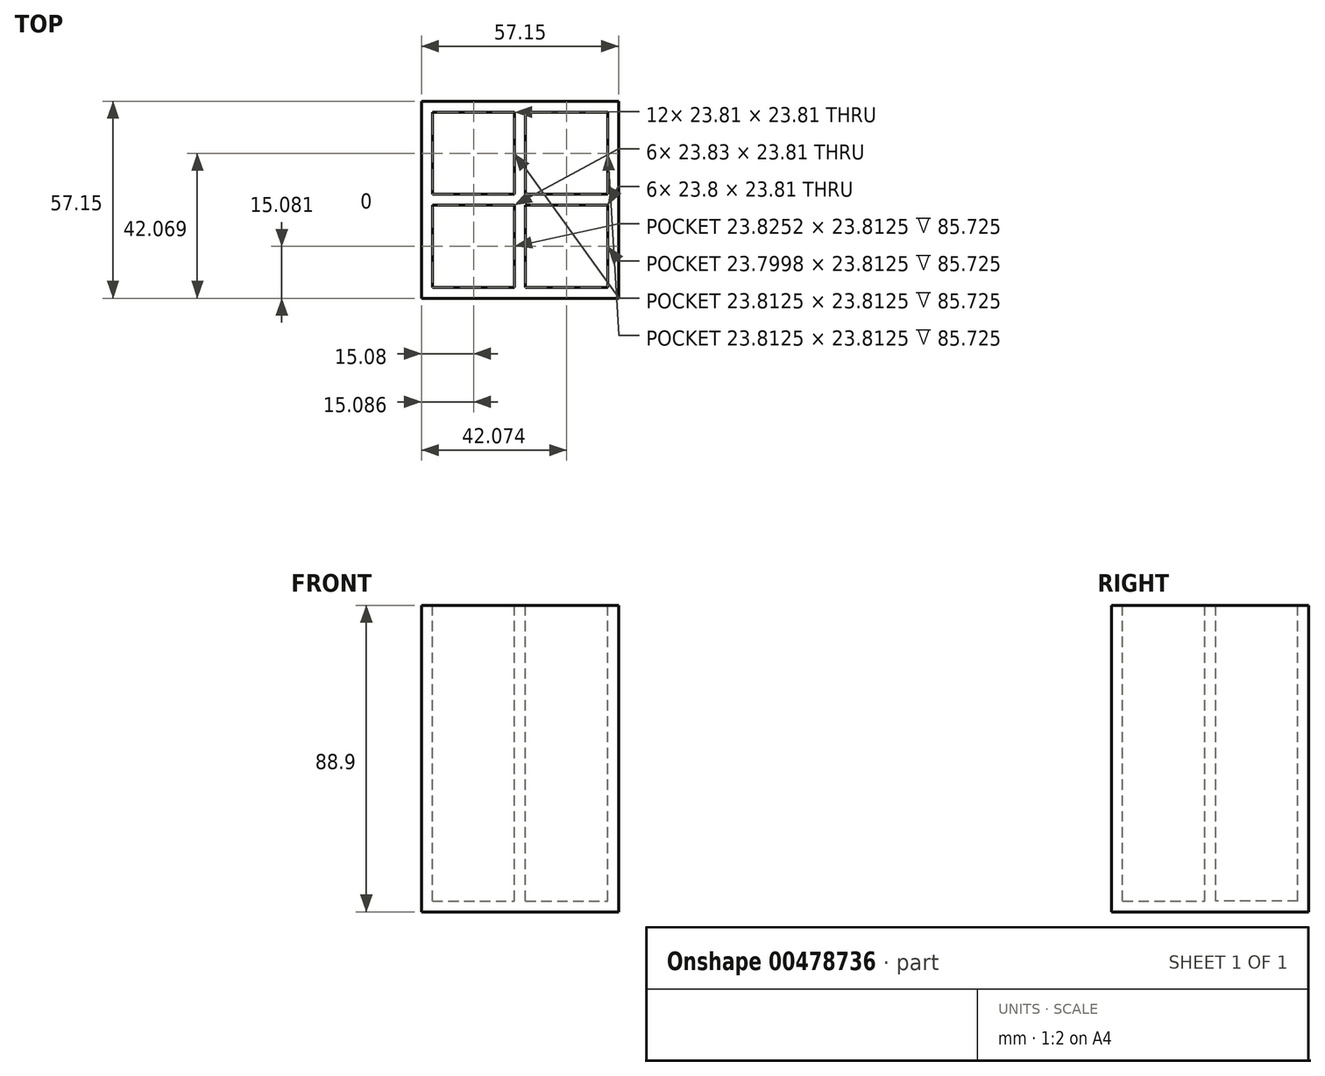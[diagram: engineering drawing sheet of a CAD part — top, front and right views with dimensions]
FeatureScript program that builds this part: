
annotation { "Feature Type Name" : "Feature", "Feature Type Description" : "" }
export const myFeature = defineFeature(function(context is Context, id is Id, definition is map)
    precondition{}
    {
        {
            var Q0;
            Q0=qCreatedBy(makeId("Front.planeOp"),FACE);
            var sketch = newSketch(context, id + "F0", { "sketchPlane" : qUnion([Q0])});
            skLineSegment(sketch, "E0.bottom", {"start": v(-40.41, 67.88) * mm, "end": v(16.74, 67.88) * mm});
            skLineSegment(sketch, "E0.top", {"start": v(-40.41, -21.02) * mm, "end": v(16.74, -21.02) * mm});
            skLineSegment(sketch, "E0.left", {"start": v(-40.41, 67.88) * mm, "end": v(-40.41, -21.02) * mm});
            skLineSegment(sketch, "E0.right", {"start": v(16.74, 67.88) * mm, "end": v(16.74, -21.02) * mm});
            skSolve(sketch);
        }
        {
            var Q0;
            Q0 = qSketchRegion(id + "F0", true);
            extrude(context, id + "F1", {"entities" : qUnion([Q0]), "depth" : 57.15 * mm});
        }
        {
            var Q0;
            Q0=makeQuery(id+"F1.opExtrude","SWEPT_FACE",FACE,{"disambiguationData":[OSD([sQuery(id+"F0.wireOp",EDGE,"E0.bottom")])]});
            var sketch = newSketch(context, id + "F2", { "sketchPlane" : qUnion([Q0])});
            skLineSegment(sketch, "E1.bottom", {"start": v(-37.24, -53.98) * mm, "end": v(-13.41, -53.98) * mm});
            skLineSegment(sketch, "E1.top", {"start": v(-37.24, -30.16) * mm, "end": v(-13.41, -30.16) * mm});
            skLineSegment(sketch, "E1.left", {"start": v(-37.24, -53.98) * mm, "end": v(-37.24, -30.16) * mm});
            skLineSegment(sketch, "E1.right", {"start": v(-13.41, -53.98) * mm, "end": v(-13.41, -30.16) * mm});
            skSolve(sketch);
        }
        {
            var Q0;
            Q0 = qSketchRegion(id + "F2", true);
            extrude(context, id + "F3", {"entities" : qUnion([Q0]), "operationType" : NewBodyOperationType.REMOVE, "oppositeDirection" : true, "depth" : 85.72 * mm});
        }
        {
            var Q0;
            Q0=makeQuery(id+"F1.opExtrude","SWEPT_FACE",FACE,{"disambiguationData":[OSD([sQuery(id+"F0.wireOp",EDGE,"E0.bottom")])]});
            var sketch = newSketch(context, id + "F4", { "sketchPlane" : qUnion([Q0])});
            skLineSegment(sketch, "E2.bottom", {"start": v(-10.24, -53.98) * mm, "end": v(13.56, -53.98) * mm});
            skLineSegment(sketch, "E2.top", {"start": v(-10.24, -30.16) * mm, "end": v(13.56, -30.16) * mm});
            skLineSegment(sketch, "E2.left", {"start": v(-10.24, -53.98) * mm, "end": v(-10.24, -30.16) * mm});
            skLineSegment(sketch, "E2.right", {"start": v(13.56, -53.98) * mm, "end": v(13.56, -30.16) * mm});
            skSolve(sketch);
        }
        {
            var Q0;
            Q0 = qSketchRegion(id + "F4", true);
            extrude(context, id + "F5", {"entities" : qUnion([Q0]), "operationType" : NewBodyOperationType.REMOVE, "oppositeDirection" : true, "depth" : 85.72 * mm});
        }
        {
            var Q0;
            Q0=makeQuery(id+"F1.opExtrude","SWEPT_FACE",FACE,{"disambiguationData":[OSD([sQuery(id+"F0.wireOp",EDGE,"E0.bottom")])]});
            var sketch = newSketch(context, id + "F6", { "sketchPlane" : qUnion([Q0])});
            skLineSegment(sketch, "E3.bottom", {"start": v(-37.24, -3.18) * mm, "end": v(-13.42, -3.18) * mm});
            skLineSegment(sketch, "E3.top", {"start": v(-37.24, -26.99) * mm, "end": v(-13.42, -26.99) * mm});
            skLineSegment(sketch, "E3.left", {"start": v(-37.24, -3.18) * mm, "end": v(-37.24, -26.99) * mm});
            skLineSegment(sketch, "E3.right", {"start": v(-13.42, -3.18) * mm, "end": v(-13.42, -26.99) * mm});
            skSolve(sketch);
        }
        {
            var Q0;
            Q0 = qSketchRegion(id + "F6", true);
            extrude(context, id + "F7", {"entities" : qUnion([Q0]), "operationType" : NewBodyOperationType.REMOVE, "oppositeDirection" : true, "depth" : 85.72 * mm});
        }
        {
            var Q0;
            Q0=makeQuery(id+"F1.opExtrude","SWEPT_FACE",FACE,{"disambiguationData":[OSD([sQuery(id+"F0.wireOp",EDGE,"E0.bottom")])]});
            var sketch = newSketch(context, id + "F8", { "sketchPlane" : qUnion([Q0])});
            skLineSegment(sketch, "E4.bottom", {"start": v(-10.25, -3.18) * mm, "end": v(13.56, -3.18) * mm});
            skLineSegment(sketch, "E4.top", {"start": v(-10.25, -26.99) * mm, "end": v(13.56, -26.99) * mm});
            skLineSegment(sketch, "E4.left", {"start": v(-10.25, -3.18) * mm, "end": v(-10.25, -26.99) * mm});
            skLineSegment(sketch, "E4.right", {"start": v(13.56, -3.17) * mm, "end": v(13.56, -26.99) * mm});
            skSolve(sketch);
        }
        {
            var Q0;
            Q0 = qSketchRegion(id + "F8", true);
            extrude(context, id + "F9", {"entities" : qUnion([Q0]), "operationType" : NewBodyOperationType.REMOVE, "oppositeDirection" : true, "depth" : 85.72 * mm});
        }
    });
